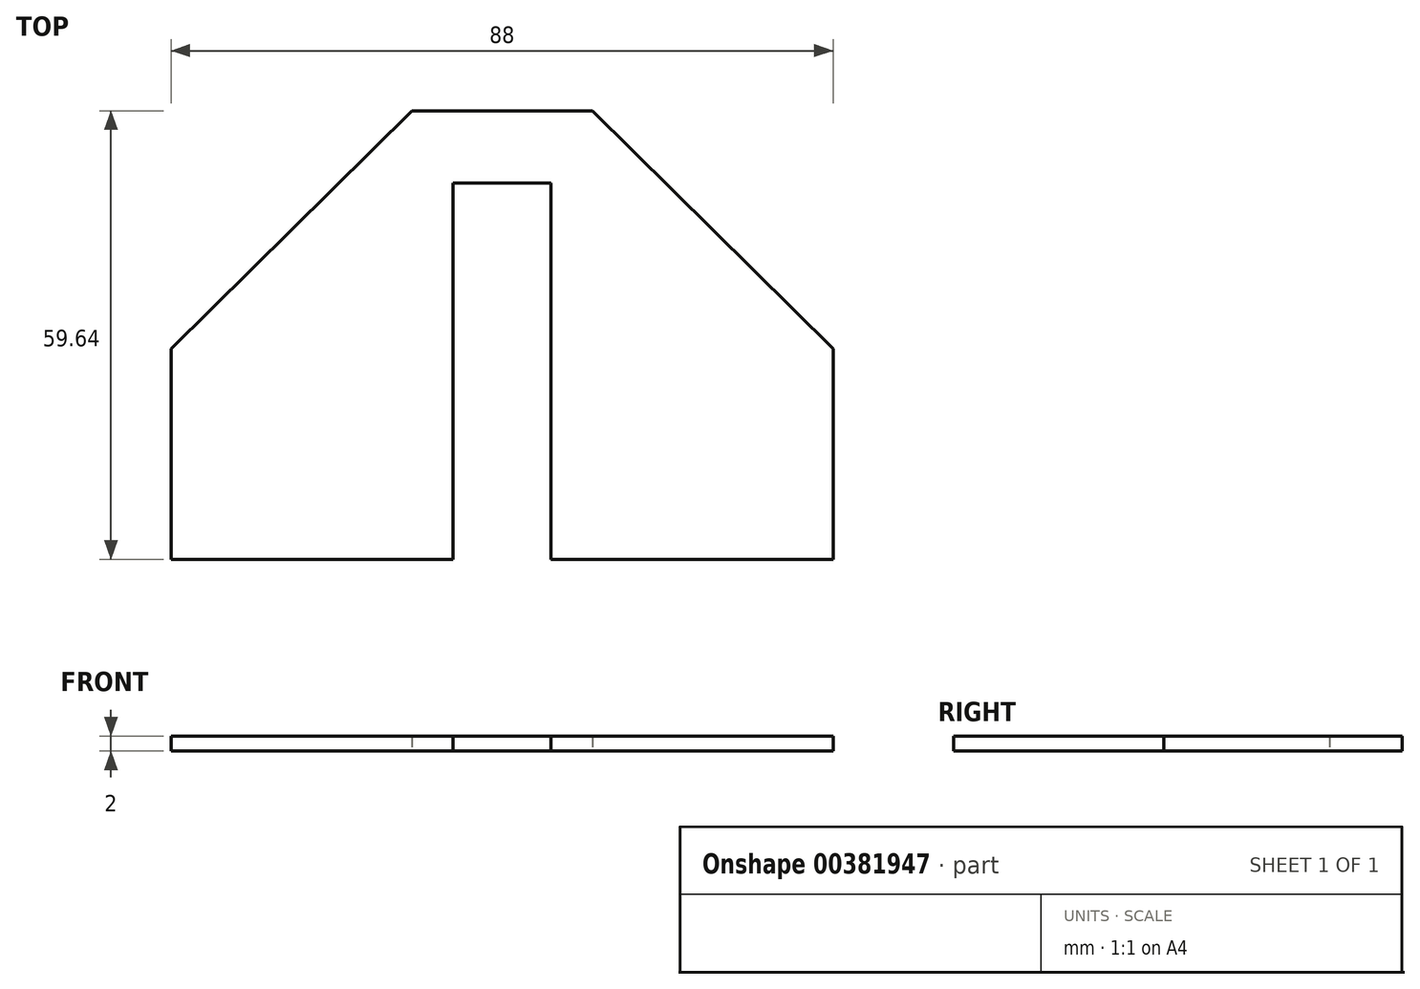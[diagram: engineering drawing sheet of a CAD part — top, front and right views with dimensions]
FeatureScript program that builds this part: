
annotation { "Feature Type Name" : "Feature", "Feature Type Description" : "" }
export const myFeature = defineFeature(function(context is Context, id is Id, definition is map)
    precondition{}
    {
        {
            var Q0;
            Q0=qCreatedBy(makeId("Top.planeOp"),FACE);
            var sketch = newSketch(context, id + "F0", { "sketchPlane" : qUnion([Q0])});
            skLineSegment(sketch, "E0", {"start": v(0, 0) * mm, "end": v(37.5, 0) * mm});
            skLineSegment(sketch, "E1", {"start": v(37.5, 0) * mm, "end": v(37.5, 28) * mm});
            skLineSegment(sketch, "E2", {"start": v(-6.5, 59.64) * mm, "end": v(5.5, 59.64) * mm});
            skLineSegment(sketch, "E3", {"start": v(5.5, 59.64) * mm, "end": v(37.5, 28) * mm});
            skLineSegment(sketch, "E4", {"start": v(0, 0) * mm, "end": v(0, 50) * mm});
            skLineSegment(sketch, "E5", {"start": v(0, 50) * mm, "end": v(-13, 50) * mm});
            skLineSegment(sketch, "E6", {"start": v(-13, 50) * mm, "end": v(-13, 0) * mm});
            skLineSegment(sketch, "E7", {"start": v(-13, 0) * mm, "end": v(-50.5, 0) * mm});
            skLineSegment(sketch, "E8", {"start": v(-50.5, 0) * mm, "end": v(-50.5, 28) * mm});
            skLineSegment(sketch, "E9", {"start": v(-50.5, 28) * mm, "end": v(-18.5, 59.64) * mm});
            skLineSegment(sketch, "E10", {"start": v(-18.5, 59.64) * mm, "end": v(-6.5, 59.64) * mm});
            skSolve(sketch);
        }
        {
            var Q0;
            Q0 = qSketchRegion(id + "F0", true);
            extrude(context, id + "F1", {"entities" : qUnion([Q0]), "depth" : 2 * mm});
        }
    });
